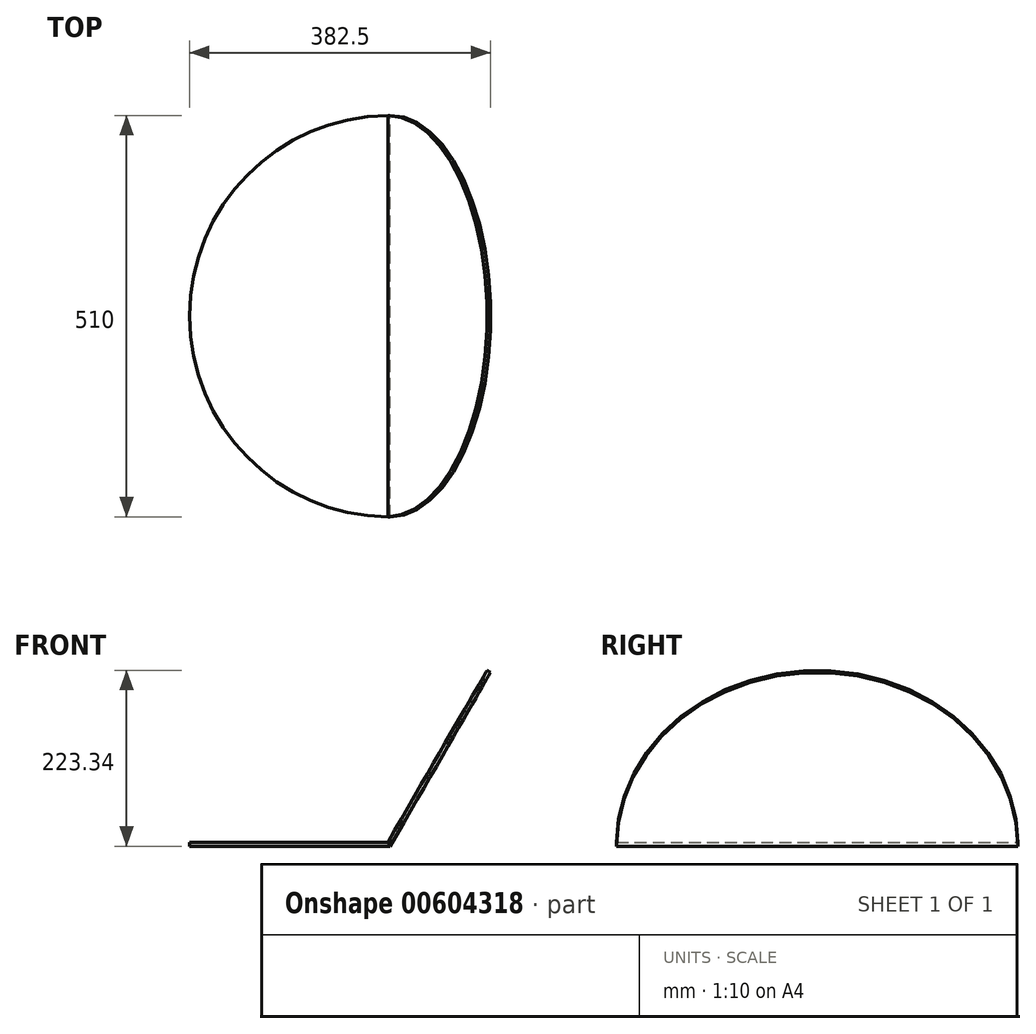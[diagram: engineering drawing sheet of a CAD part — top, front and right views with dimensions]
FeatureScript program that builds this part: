
annotation { "Feature Type Name" : "Feature", "Feature Type Description" : "" }
export const myFeature = defineFeature(function(context is Context, id is Id, definition is map)
    precondition{}
    {
        {
            var Q0;
            Q0=qCreatedBy(makeId("Front.planeOp"),FACE);
            var sketch = newSketch(context, id + "F0", { "sketchPlane" : qUnion([Q0])});
            skLineSegment(sketch, "E0", {"start": v(0, 0) * mm, "end": v(150, 259.8) * mm});
            skLineSegment(sketch, "E1", {"start": v(150, 259.8) * mm, "end": v(145.67, 262.3) * mm});
            skLineSegment(sketch, "E2", {"start": v(145.67, 262.3) * mm, "end": v(-2.89, 5) * mm});
            skLineSegment(sketch, "E3", {"start": v(-2.89, 5) * mm, "end": v(-300, 5) * mm});
            skLineSegment(sketch, "E4", {"start": v(-300, 5) * mm, "end": v(-300, 0) * mm});
            skLineSegment(sketch, "E5", {"start": v(-300, 0) * mm, "end": v(0, 0) * mm});
            skSolve(sketch);
        }
        {
            var Q0;
            Q0 = qSketchRegion(id + "F0", true);
            extrude(context, id + "F1", {"entities" : qUnion([Q0]), "depth" : 300 * mm, "offsetDistance" : 25 * mm, "hasSecondDirection" : true, "secondDirectionOppositeDirection" : true, "secondDirectionDepth" : 300 * mm});
        }
        {
            var Q0;
            Q0=qCreatedBy(makeId("Top.planeOp"),FACE);
            var sketch = newSketch(context, id + "F2", { "sketchPlane" : qUnion([Q0])});
            skCircle(sketch, "E6", {"center": v(0, 0) * mm, "radius": 255 * mm});
            skSolve(sketch);
        }
        {
            var Q0;
            Q0 = qSketchRegion(id + "F2", true);
            extrude(context, id + "F3", {"entities" : qUnion([Q0]), "operationType" : NewBodyOperationType.INTERSECT, "depth" : 500 * mm, "offsetDistance" : 25 * mm});
        }
        {
            var Q0;
            Q0=makeQuery(id+"F1.opExtrude","SWEPT_FACE",FACE,{"disambiguationData":[OSD([sQuery(id+"F0.wireOp",EDGE,"E0")])]});
            var sketch = newSketch(context, id + "F4", { "sketchPlane" : qUnion([Q0])});
            skCircle(sketch, "E7", {"center": v(0, 0) * mm, "radius": 255 * mm});
            skSolve(sketch);
        }
        {
            var Q0;
            Q0 = qSketchRegion(id + "F4", true);
            extrude(context, id + "F5", {"entities" : qUnion([Q0]), "operationType" : NewBodyOperationType.INTERSECT, "oppositeDirection" : true, "depth" : 500 * mm, "offsetDistance" : 25 * mm});
        }
    });
